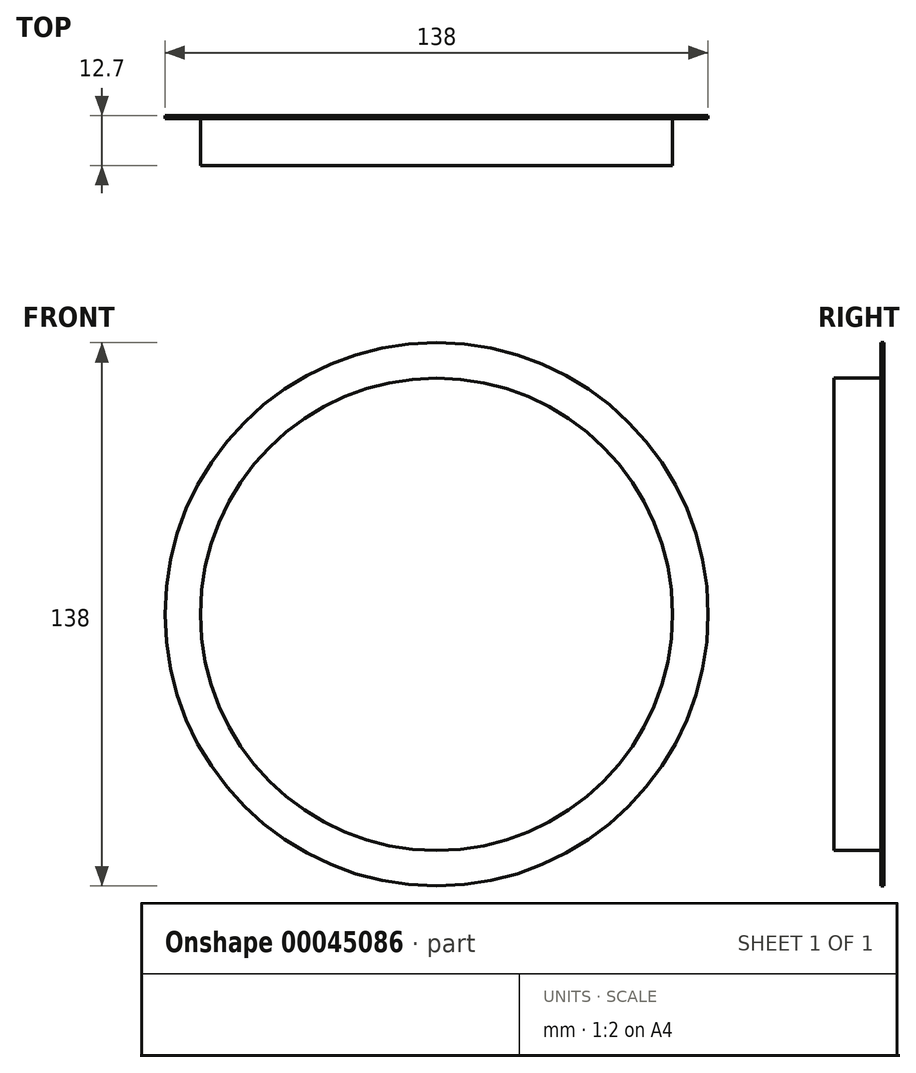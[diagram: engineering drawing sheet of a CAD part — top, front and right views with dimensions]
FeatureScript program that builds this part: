
annotation { "Feature Type Name" : "Feature", "Feature Type Description" : "" }
export const myFeature = defineFeature(function(context is Context, id is Id, definition is map)
    precondition{}
    {
        {
            var Q0;
            Q0=qCreatedBy(makeId("Front.planeOp"),FACE);
            var sketch = newSketch(context, id + "F0", { "sketchPlane" : qUnion([Q0])});
            skCircle(sketch, "E0", {"center": v(0, 0) * mm, "radius": 69 * mm});
            skSolve(sketch);
        }
        {
            var Q0;
            Q0 = qSketchRegion(id + "F0", true);
            extrude(context, id + "F1", {"entities" : qUnion([Q0]), "depth" : 0.76 * mm});
        }
        {
            var Q0;
            Q0=makeQuery(id+"F1.opExtrude","CAP_FACE",FACE,{"disambiguationData":[OSD([sQuery(id+"F0.wireOp",EDGE,"E0")])],"isStart":true});
            var sketch = newSketch(context, id + "F2", { "sketchPlane" : qUnion([Q0])});
            skCircle(sketch, "E1", {"center": v(0, 0) * mm, "radius": 60 * mm});
            skSolve(sketch);
        }
        {
            var Q0;
            Q0 = qSketchRegion(id + "F2", true);
            extrude(context, id + "F3", {"entities" : qUnion([Q0]), "operationType" : NewBodyOperationType.ADD, "oppositeDirection" : true, "depth" : 12.7 * mm});
        }
    });
